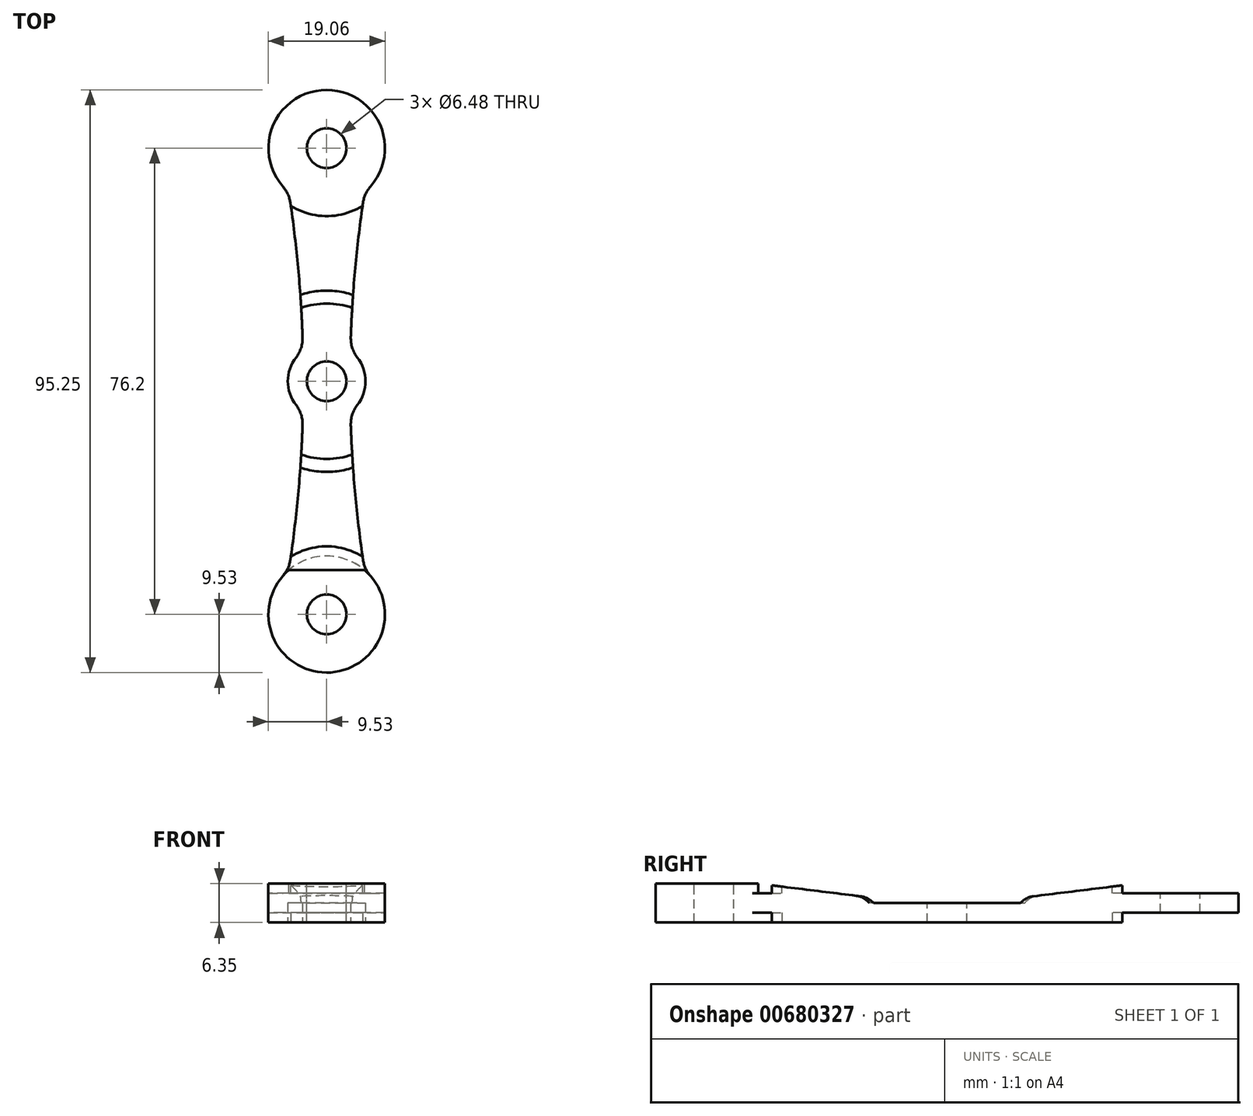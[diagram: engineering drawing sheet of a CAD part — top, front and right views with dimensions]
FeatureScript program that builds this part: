
annotation { "Feature Type Name" : "Feature", "Feature Type Description" : "" }
export const myFeature = defineFeature(function(context is Context, id is Id, definition is map)
    precondition{}
    {
        {
            var Q0;
            Q0=qCreatedBy(makeId("Top.planeOp"),FACE);
            var sketch = newSketch(context, id + "F0", { "sketchPlane" : qUnion([Q0])});
            skLineSegment(sketch, "E0.bottom", {"start": v(9.52, 47.63) * mm, "end": v(-9.53, 47.63) * mm});
            skLineSegment(sketch, "E0.top", {"start": v(9.52, -47.63) * mm, "end": v(-9.53, -47.63) * mm});
            skLineSegment(sketch, "E0.left", {"start": v(9.52, 47.63) * mm, "end": v(9.52, -47.63) * mm});
            skLineSegment(sketch, "E0.right", {"start": v(-9.52, 47.63) * mm, "end": v(-9.53, -47.63) * mm});
            skPoint(sketch, "E0.middle", {"position": v(0, 0) * mm});
            skCircle(sketch, "E1", {"center": v(0, 38.1) * mm, "radius": 9.53 * mm});
            skCircle(sketch, "E2", {"center": v(0, -38.1) * mm, "radius": 9.52 * mm});
            skCircle(sketch, "E3", {"center": v(0, 0) * mm, "radius": 6.35 * mm});
            skArc(sketch, "E4", {"start": v(-9.53, -47.62) * mm, "mid": v(-3.81, 0) * mm, "end": v(-9.53, 47.63) * mm});
            skArc(sketch, "E5", {"start": v(9.53, 47.62) * mm, "mid": v(3.81, 0) * mm, "end": v(9.53, -47.62) * mm});
            skSolve(sketch);
        }
        {
            var Q0;
            {var subQ0=sQuery(id+"F0.wireOp",EDGE,"E4");var subQ1=sQuery(id+"F0.wireOp",EDGE,"E3");var subQ2=makeQuery(id+"F0.imprint","INTERSECT",VERTEX,{"disambiguationData":[OD(0.0)],"derivedFrom":[subQ1,subQ0]});Q0=makeQuery(id+"F0.imprint","IMPRINT",FACE,{"disambiguationData":[TD([[makeQuery(id+"F0.imprint","IMPRINT",EDGE,{"disambiguationData":[TD([[subQ2,1.0]])],"derivedFrom":subQ1}),1.0]])]});}
            var Q1;
            {var subQ0=sQuery(id+"F0.wireOp",EDGE,"E5");var subQ1=sQuery(id+"F0.wireOp",EDGE,"E3");var subQ2=makeQuery(id+"F0.imprint","INTERSECT",VERTEX,{"disambiguationData":[OD(0.0)],"derivedFrom":[subQ1,subQ0]});Q1=makeQuery(id+"F0.imprint","IMPRINT",FACE,{"disambiguationData":[TD([[makeQuery(id+"F0.imprint","IMPRINT",EDGE,{"disambiguationData":[TD([[subQ2,1.0]])],"derivedFrom":subQ1}),1.0]])]});}
            var Q2;
            {var subQ0=sQuery(id+"F0.wireOp",EDGE,"E4");var subQ1=sQuery(id+"F0.wireOp",EDGE,"E3");var subQ2=makeQuery(id+"F0.imprint","INTERSECT",VERTEX,{"disambiguationData":[OD(0.0)],"derivedFrom":[subQ1,subQ0]});Q2=makeQuery(id+"F0.imprint","IMPRINT",FACE,{"disambiguationData":[TD([[makeQuery(id+"F0.imprint","IMPRINT",EDGE,{"disambiguationData":[TD([[subQ2,-1.0]])],"derivedFrom":subQ1}),1.0]])]});}
            var Q3;
            {var subQ0=sQuery(id+"F0.wireOp",EDGE,"E4");var subQ1=sQuery(id+"F0.wireOp",EDGE,"E1");var subQ2=makeQuery(id+"F0.imprint","INTERSECT",VERTEX,{"disambiguationData":[OD(1.0)],"derivedFrom":[subQ1,subQ0]});Q3=makeQuery(id+"F0.imprint","IMPRINT",FACE,{"disambiguationData":[TD([[makeQuery(id+"F0.imprint","IMPRINT",EDGE,{"disambiguationData":[TD([[subQ2,-1.0]])],"derivedFrom":subQ1}),-1.0]])]});}
            var Q4;
            {var subQ0=sQuery(id+"F0.wireOp",EDGE,"E5");var subQ1=sQuery(id+"F0.wireOp",EDGE,"E2");var subQ2=makeQuery(id+"F0.imprint","INTERSECT",VERTEX,{"disambiguationData":[OD(0.0)],"derivedFrom":[subQ1,subQ0]});Q4=makeQuery(id+"F0.imprint","IMPRINT",FACE,{"disambiguationData":[TD([[makeQuery(id+"F0.imprint","IMPRINT",EDGE,{"disambiguationData":[TD([[subQ2,-1.0]])],"derivedFrom":subQ1}),-1.0]])]});}
            var Q5;
            {var subQ0=sQuery(id+"F0.wireOp",EDGE,"E1");var subQ1=makeQuery(id+"F0.imprint","INTERSECT",VERTEX,{"derivedFrom":[sQuery(id+"F0.wireOp",EDGE,"E0.left"),subQ0]});Q5=makeQuery(id+"F0.imprint","IMPRINT",FACE,{"disambiguationData":[TD([[makeQuery(id+"F0.imprint","IMPRINT",EDGE,{"disambiguationData":[TD([[subQ1,-1.0]])],"derivedFrom":subQ0}),1.0]])]});}
            var Q6;
            {var subQ0=sQuery(id+"F0.wireOp",EDGE,"E1");var subQ1=makeQuery(id+"F0.imprint","INTERSECT",VERTEX,{"derivedFrom":[sQuery(id+"F0.wireOp",EDGE,"E0.right"),subQ0]});Q6=makeQuery(id+"F0.imprint","IMPRINT",FACE,{"disambiguationData":[TD([[makeQuery(id+"F0.imprint","IMPRINT",EDGE,{"disambiguationData":[TD([[subQ1,1.0]])],"derivedFrom":subQ0}),1.0]])]});}
            var Q7;
            {var subQ0=sQuery(id+"F0.wireOp",EDGE,"E2");var subQ1=makeQuery(id+"F0.imprint","INTERSECT",VERTEX,{"derivedFrom":[sQuery(id+"F0.wireOp",EDGE,"E0.left"),subQ0]});Q7=makeQuery(id+"F0.imprint","IMPRINT",FACE,{"disambiguationData":[TD([[makeQuery(id+"F0.imprint","IMPRINT",EDGE,{"disambiguationData":[TD([[subQ1,-1.0]])],"derivedFrom":subQ0}),1.0]])]});}
            var Q8;
            {var subQ0=sQuery(id+"F0.wireOp",EDGE,"E2");var subQ1=makeQuery(id+"F0.imprint","INTERSECT",VERTEX,{"derivedFrom":[sQuery(id+"F0.wireOp",EDGE,"E0.right"),subQ0]});Q8=makeQuery(id+"F0.imprint","IMPRINT",FACE,{"disambiguationData":[TD([[makeQuery(id+"F0.imprint","IMPRINT",EDGE,{"disambiguationData":[TD([[subQ1,1.0]])],"derivedFrom":subQ0}),1.0]])]});}
            var Q9;
            {var subQ1=sQuery(id+"F0.wireOp",EDGE,"E1");var subQ4=makeQuery(id+"F0.imprint","INTERSECT",VERTEX,{"derivedFrom":[sQuery(id+"F0.wireOp",EDGE,"E0.bottom"),subQ1]});Q9=makeQuery(id+"F0.imprint","IMPRINT",FACE,{"disambiguationData":[TD([[makeQuery(id+"F0.imprint","IMPRINT",EDGE,{"disambiguationData":[TD([[subQ4,1.0]])],"derivedFrom":subQ1}),1.0]])]});}
            var Q10;
            {var subQ1=sQuery(id+"F0.wireOp",EDGE,"E2");var subQ4=sQuery(id+"F0.wireOp",EDGE,"E5");var subQ5=makeQuery(id+"F0.imprint","INTERSECT",VERTEX,{"disambiguationData":[OD(0.0)],"derivedFrom":[subQ1,subQ4]});Q10=makeQuery(id+"F0.imprint","IMPRINT",FACE,{"disambiguationData":[TD([[makeQuery(id+"F0.imprint","IMPRINT",EDGE,{"disambiguationData":[TD([[subQ5,-1.0]])],"derivedFrom":subQ1}),1.0]])]});}
            extrude(context, id + "F1", {"entities" : qUnion([Q0, Q1, Q2, Q3, Q4, Q5, Q6, Q7, Q8, Q9, Q10]), "depth" : 6.35 * mm, "offsetDistance" : 25.4 * mm});
        }
        {
            var Q0;
            Q0=makeQuery(id+"F1.opExtrude","CAP_FACE",FACE,{"disambiguationData":[OSD([sQuery(id+"F0.wireOp",EDGE,"E1"),sQuery(id+"F0.wireOp",EDGE,"E2"),sQuery(id+"F0.wireOp",EDGE,"E3"),sQuery(id+"F0.wireOp",EDGE,"E4"),sQuery(id+"F0.wireOp",EDGE,"E5")])],"isStart":false});
            var sketch = newSketch(context, id + "F2", { "sketchPlane" : qUnion([Q0])});
            skCircle(sketch, "E6", {"center": v(0, 38.1) * mm, "radius": 3.24 * mm});
            skCircle(sketch, "E7", {"center": v(0, 0) * mm, "radius": 3.24 * mm});
            skCircle(sketch, "E8", {"center": v(0, -38.1) * mm, "radius": 3.24 * mm});
            skSolve(sketch);
        }
        {
            var Q0;
            Q0=qSketchRegion(id+"F2",true);
            extrude(context, id + "F3", {"entities" : qUnion([Q0]), "operationType" : NewBodyOperationType.REMOVE, "endBound" : BoundingType.THROUGH_ALL, "oppositeDirection" : true, "depth" : 25.4 * mm, "offsetDistance" : 25.4 * mm});
        }
        {
            var Q0;
            Q0=qCreatedBy(makeId("Right.planeOp"),FACE);
            var sketch = newSketch(context, id + "F4", { "sketchPlane" : qUnion([Q0])});
            skPoint(sketch, "E9.0", {"position": v(-30.86, 6.35) * mm});
            skPoint(sketch, "E10.0", {"position": v(30.86, 6.35) * mm});
            skLineSegment(sketch, "E11", {"start": v(-30.86, 6.35) * mm, "end": v(30.86, 6.35) * mm});
            skPoint(sketch, "E12.0", {"position": v(-5.03, 3.18) * mm});
            skPoint(sketch, "E13.0", {"position": v(5.03, 3.18) * mm});
            skLineSegment(sketch, "E14", {"start": v(-30.86, 6.35) * mm, "end": v(-5.03, 3.18) * mm});
            skLineSegment(sketch, "E15", {"start": v(5.03, 3.18) * mm, "end": v(30.86, 6.35) * mm});
            skLineSegment(sketch, "E16", {"start": v(-5.03, 3.18) * mm, "end": v(5.03, 3.18) * mm});
            skSolve(sketch);
        }
        {
            var Q0;
            Q0=qSketchRegion(id+"F4",true);
            extrude(context, id + "F5", {"entities" : qUnion([Q0]), "operationType" : NewBodyOperationType.REMOVE, "oppositeDirection" : true, "depth" : 25.4 * mm, "offsetDistance" : 25.4 * mm, "hasSecondDirection" : true, "secondDirectionOppositeDirection" : false, "secondDirectionDepth" : 25.4 * mm});
        }
        {
            var Q0;
            Q0=makeQuery(id+"F5.boolean.opBoolean","COPY",EDGE,{"derivedFrom":makeQuery(id+"F5.opExtrude","SWEPT_EDGE",EDGE,{"disambiguationData":[OSD([sQuery(id+"F4.wireOp",EDGE,"E11"),sQuery(id+"F4.wireOp",EDGE,"E14")])]})});
            var Q1;
            Q1=makeQuery(id+"F5.boolean.opBoolean","COPY",EDGE,{"derivedFrom":makeQuery(id+"F5.opExtrude","SWEPT_EDGE",EDGE,{"disambiguationData":[OSD([sQuery(id+"F4.wireOp",EDGE,"E11"),sQuery(id+"F4.wireOp",EDGE,"E15")])]})});
            var Q2;
            Q2=makeQuery(id+"F5.boolean.opBoolean","COPY",EDGE,{"derivedFrom":makeQuery(id+"F5.opExtrude","SWEPT_EDGE",EDGE,{"disambiguationData":[OSD([sQuery(id+"F4.wireOp",EDGE,"E14"),sQuery(id+"F4.wireOp",EDGE,"E16")])]})});
            var Q3;
            Q3=makeQuery(id+"F5.boolean.opBoolean","COPY",EDGE,{"derivedFrom":makeQuery(id+"F5.opExtrude","SWEPT_EDGE",EDGE,{"disambiguationData":[OSD([sQuery(id+"F4.wireOp",EDGE,"E15"),sQuery(id+"F4.wireOp",EDGE,"E16")])]})});
            var Q4;
            {var subQ0=sQuery(id+"F0.wireOp",EDGE,"E5");var subQ1=sQuery(id+"F0.wireOp",EDGE,"E3");Q4=makeQuery(id+"F1.opExtrude","SWEPT_EDGE",EDGE,{"disambiguationData":[OSD([subQ1,subQ0]),TDD([makeQuery(id+"F0.imprint","INTERSECT",VERTEX,{"disambiguationData":[OD(0.0)],"derivedFrom":[subQ1,subQ0]})])]});}
            var Q5;
            {var subQ0=sQuery(id+"F0.wireOp",EDGE,"E5");var subQ1=sQuery(id+"F0.wireOp",EDGE,"E3");Q5=makeQuery(id+"F1.opExtrude","SWEPT_EDGE",EDGE,{"disambiguationData":[OSD([subQ1,subQ0]),TDD([makeQuery(id+"F0.imprint","INTERSECT",VERTEX,{"disambiguationData":[OD(1.0)],"derivedFrom":[subQ1,subQ0]})])]});}
            var Q6;
            {var subQ0=sQuery(id+"F0.wireOp",EDGE,"E4");var subQ1=sQuery(id+"F0.wireOp",EDGE,"E3");Q6=makeQuery(id+"F1.opExtrude","SWEPT_EDGE",EDGE,{"disambiguationData":[OSD([subQ1,subQ0]),TDD([makeQuery(id+"F0.imprint","INTERSECT",VERTEX,{"disambiguationData":[OD(1.0)],"derivedFrom":[subQ1,subQ0]})])]});}
            var Q7;
            {var subQ0=sQuery(id+"F0.wireOp",EDGE,"E4");var subQ1=sQuery(id+"F0.wireOp",EDGE,"E3");Q7=makeQuery(id+"F1.opExtrude","SWEPT_EDGE",EDGE,{"disambiguationData":[OSD([subQ1,subQ0]),TDD([makeQuery(id+"F0.imprint","INTERSECT",VERTEX,{"disambiguationData":[OD(0.0)],"derivedFrom":[subQ1,subQ0]})])]});}
            var Q8;
            Q8=makeQuery(id+"F1.opExtrude","SWEPT_EDGE",EDGE,{"disambiguationData":[OSD([sQuery(id+"F0.wireOp",EDGE,"E2"),sQuery(id+"F0.wireOp",EDGE,"E4")])]});
            var Q9;
            Q9=makeQuery(id+"F1.opExtrude","SWEPT_EDGE",EDGE,{"disambiguationData":[OSD([sQuery(id+"F0.wireOp",EDGE,"E1"),sQuery(id+"F0.wireOp",EDGE,"E4")])]});
            var Q10;
            Q10=makeQuery(id+"F1.opExtrude","SWEPT_EDGE",EDGE,{"disambiguationData":[OSD([sQuery(id+"F0.wireOp",EDGE,"E1"),sQuery(id+"F0.wireOp",EDGE,"E5")])]});
            var Q11;
            Q11=makeQuery(id+"F1.opExtrude","SWEPT_EDGE",EDGE,{"disambiguationData":[OSD([sQuery(id+"F0.wireOp",EDGE,"E2"),sQuery(id+"F0.wireOp",EDGE,"E5")])]});
            fillet(context, id + "F6", {"entities" : qUnion([Q0, Q1, Q2, Q3, Q4, Q5, Q6, Q7, Q8, Q9, Q10, Q11]), "radius" : 5.08 * mm, "tangentPropagation" : true, "allowEdgeOverflow" : false});
        }
        {
            var Q0;
            {var subQ0=sQuery(id+"F0.wireOp",EDGE,"E5");var subQ1=sQuery(id+"F0.wireOp",EDGE,"E2");var subQ2=sQuery(id+"F0.wireOp",EDGE,"E3");var subQ3=sQuery(id+"F0.wireOp",EDGE,"E4");Q0=makeQuery(id+"F5.boolean.opBoolean","SPLIT",FACE,{"disambiguationData":[TD([makeQuery(id+"F1.opExtrude","SWEPT_FACE",FACE,{"disambiguationData":[OSD([subQ1])]})])],"derivedFrom":makeQuery(id+"F1.opExtrude","CAP_FACE",FACE,{"disambiguationData":[OSD([sQuery(id+"F0.wireOp",EDGE,"E1"),subQ1,subQ2,subQ3,subQ0])],"isStart":false})});}
            var sketch = newSketch(context, id + "F7", { "sketchPlane" : qUnion([Q0])});
            skCircle(sketch, "E17", {"center": v(0, -38.1) * mm, "radius": 9.52 * mm});
            skArc(sketch, "E18.0", {"start": v(7.15, 31.8) * mm, "mid": v(0, 47.63) * mm, "end": v(-7.15, 31.8) * mm});
            skCircle(sketch, "E19", {"center": v(0, 38.1) * mm, "radius": 9.53 * mm});
            skCircle(sketch, "E20", {"center": v(0, -38.1) * mm, "radius": 11.11 * mm});
            skCircle(sketch, "E21", {"center": v(0, 38.1) * mm, "radius": 11.11 * mm});
            skSolve(sketch);
        }
        {
            var Q0;
            Q0 = qSketchRegion(id + "F7", true);
            var Q1;
            {var subQ0=sQuery(id+"F2.wireOp",EDGE,"E8");Q1=makeQuery(id+"F7.imprint","IMPRINT",FACE,{"disambiguationData":[TD([[makeQuery(id+"F7.imprint","IMPRINT",EDGE,{"derivedFrom":makeQuery(id+"F3.boolean.opBoolean","COPY",EDGE,{"derivedFrom":makeQuery(id+"F3.opExtrude","CAP_EDGE",EDGE,{"disambiguationData":[OSD([subQ0])],"isStart":true})})}),-1.0]])]});}
            var Q2;
            {var subQ0=sQuery(id+"F7.wireOp",EDGE,"E17");var subQ1=sQuery(id+"F0.wireOp",EDGE,"E5");var subQ2=sQuery(id+"F0.wireOp",EDGE,"E2");var subQ3=sQuery(id+"F0.wireOp",EDGE,"E3");var subQ4=sQuery(id+"F0.wireOp",EDGE,"E4");var subQ5=sQuery(id+"F4.wireOp",EDGE,"E14");var subQ6=makeQuery(id+"F6.opFillet","BLEND_EDGE",EDGE,{"blendedFrom":[makeQuery(id+"F5.boolean.opBoolean","COPY",EDGE,{"derivedFrom":makeQuery(id+"F5.opExtrude","SWEPT_EDGE",EDGE,{"disambiguationData":[OSD([sQuery(id+"F4.wireOp",EDGE,"E11"),subQ5])]})}),makeQuery(id+"F5.boolean.opBoolean","SPLIT",FACE,{"disambiguationData":[TD([makeQuery(id+"F1.opExtrude","SWEPT_FACE",FACE,{"disambiguationData":[OSD([subQ2])]})])],"derivedFrom":makeQuery(id+"F1.opExtrude","CAP_FACE",FACE,{"disambiguationData":[OSD([sQuery(id+"F0.wireOp",EDGE,"E1"),subQ2,subQ3,subQ4,subQ1])],"isStart":false})})],"blendedInto":[makeQuery(id+"F5.boolean.opBoolean","SPLIT",FACE,{"disambiguationData":[TD([makeQuery(id+"F1.opExtrude","SWEPT_FACE",FACE,{"disambiguationData":[OSD([subQ2])]})])],"derivedFrom":makeQuery(id+"F1.opExtrude","CAP_FACE",FACE,{"disambiguationData":[OSD([sQuery(id+"F0.wireOp",EDGE,"E1"),subQ2,subQ3,subQ4,subQ1])],"isStart":false})})]});var subQ7=makeQuery(id+"F7.imprint","INTERSECT",VERTEX,{"disambiguationData":[OD(0.0)],"derivedFrom":[subQ6,subQ0]});Q2=makeQuery(id+"F7.imprint","IMPRINT",FACE,{"disambiguationData":[TD([[makeQuery(id+"F7.imprint","IMPRINT",EDGE,{"disambiguationData":[TD([[subQ7,-1.0]])],"derivedFrom":subQ0}),1.0]])]});}
            var Q3;
            {var subQ0=sQuery(id+"F7.wireOp",EDGE,"E19");var subQ1=makeQuery(id+"F7.imprint","IMPRINT",VERTEX,{"disambiguationData":[OD(0.0)],"derivedFrom":subQ0});Q3=makeQuery(id+"F7.imprint","IMPRINT",FACE,{"disambiguationData":[TD([[makeQuery(id+"F7.imprint","IMPRINT",EDGE,{"disambiguationData":[TD([[subQ1,-1.0]])],"derivedFrom":subQ0}),1.0]])]});}
            extrude(context, id + "F8", {"entities" : qUnion([Q0, Q1, Q2, Q3]), "operationType" : NewBodyOperationType.REMOVE, "oppositeDirection" : true, "depth" : 1.59 * mm, "offsetDistance" : 25.4 * mm});
        }
        {
            var Q0;
            Q0=makeQuery(id+"F1.opExtrude","CAP_FACE",FACE,{"disambiguationData":[OSD([sQuery(id+"F0.wireOp",EDGE,"E1"),sQuery(id+"F0.wireOp",EDGE,"E2"),sQuery(id+"F0.wireOp",EDGE,"E3"),sQuery(id+"F0.wireOp",EDGE,"E4"),sQuery(id+"F0.wireOp",EDGE,"E5")])],"isStart":true});
            var sketch = newSketch(context, id + "F9", { "sketchPlane" : qUnion([Q0])});
            skArc(sketch, "E22.0", {"start": v(-7.15, 31.8) * mm, "mid": v(0, 47.63) * mm, "end": v(7.15, 31.8) * mm});
            skArc(sketch, "E23.0", {"start": v(7.15, -31.8) * mm, "mid": v(0, -47.63) * mm, "end": v(-7.15, -31.8) * mm});
            skCircle(sketch, "E24", {"center": v(0, 38.1) * mm, "radius": 9.52 * mm});
            skCircle(sketch, "E25", {"center": v(0, -38.1) * mm, "radius": 9.53 * mm});
            skCircle(sketch, "E26", {"center": v(0, 38.1) * mm, "radius": 11.11 * mm});
            skCircle(sketch, "E27", {"center": v(0, -38.1) * mm, "radius": 11.11 * mm});
            skSolve(sketch);
        }
        {
            var Q0;
            Q0 = qSketchRegion(id + "F9", true);
            var Q1;
            {var subQ0=sQuery(id+"F9.wireOp",EDGE,"E24");Q1=makeQuery(id+"F9.imprint","IMPRINT",FACE,{"disambiguationData":[TD([[makeQuery(id+"F9.imprint","IMPRINT",EDGE,{"disambiguationData":[OD(0.0)],"derivedFrom":subQ0}),-1.0]])]});}
            var Q2;
            Q2=makeQuery(id+"F9.imprint","IMPRINT",FACE,{"disambiguationData":[TD([[makeQuery(id+"F9.imprint","IMPRINT",EDGE,{"derivedFrom":makeQuery(id+"F3.boolean.opBoolean","INTERSECT",EDGE,{"derivedFrom":[makeQuery(id+"F1.opExtrude","CAP_FACE",FACE,{"disambiguationData":[OSD([sQuery(id+"F0.wireOp",EDGE,"E1"),sQuery(id+"F0.wireOp",EDGE,"E2"),sQuery(id+"F0.wireOp",EDGE,"E3"),sQuery(id+"F0.wireOp",EDGE,"E4"),sQuery(id+"F0.wireOp",EDGE,"E5")])],"isStart":true}),makeQuery(id+"F3.opExtrude","SWEPT_FACE",FACE,{"disambiguationData":[OSD([sQuery(id+"F2.wireOp",EDGE,"E8")])]})]})}),-1.0]])]});
            var Q3;
            Q3=makeQuery(id+"F9.imprint","IMPRINT",FACE,{"disambiguationData":[TD([[makeQuery(id+"F9.imprint","IMPRINT",EDGE,{"derivedFrom":makeQuery(id+"F3.boolean.opBoolean","INTERSECT",EDGE,{"derivedFrom":[makeQuery(id+"F1.opExtrude","CAP_FACE",FACE,{"disambiguationData":[OSD([sQuery(id+"F0.wireOp",EDGE,"E1"),sQuery(id+"F0.wireOp",EDGE,"E2"),sQuery(id+"F0.wireOp",EDGE,"E3"),sQuery(id+"F0.wireOp",EDGE,"E4"),sQuery(id+"F0.wireOp",EDGE,"E5")])],"isStart":true}),makeQuery(id+"F3.opExtrude","SWEPT_FACE",FACE,{"disambiguationData":[OSD([sQuery(id+"F2.wireOp",EDGE,"E6")])]})]})}),-1.0]])]});
            var Q4;
            {var subQ0=sQuery(id+"F9.wireOp",EDGE,"E25");Q4=makeQuery(id+"F9.imprint","IMPRINT",FACE,{"disambiguationData":[TD([[makeQuery(id+"F9.imprint","IMPRINT",EDGE,{"disambiguationData":[OD(0.0)],"derivedFrom":subQ0}),1.0]])]});}
            extrude(context, id + "F10", {"entities" : qUnion([Q0, Q1, Q2, Q3, Q4]), "operationType" : NewBodyOperationType.REMOVE, "oppositeDirection" : true, "depth" : 1.59 * mm, "offsetDistance" : 25.4 * mm});
        }
        {
            var Q0;
            Q0=makeQuery(id+"F5.boolean.opBoolean","COPY",FACE,{"derivedFrom":makeQuery(id+"F5.opExtrude","SWEPT_FACE",FACE,{"disambiguationData":[OSD([sQuery(id+"F4.wireOp",EDGE,"E16")])]})});
            var sketch = newSketch(context, id + "F11", { "sketchPlane" : qUnion([Q0])});
            skCircle(sketch, "E28.0", {"center": v(0, 0) * mm, "radius": 3.24 * mm});
            skCircle(sketch, "E29", {"center": v(0, 0) * mm, "radius": 12.7 * mm});
            skSolve(sketch);
        }
        {
            var Q0;
            Q0 = qSketchRegion(id + "F11", true);
            extrude(context, id + "F12", {"entities" : qUnion([Q0]), "operationType" : NewBodyOperationType.REMOVE, "depth" : 25.4 * mm, "offsetDistance" : 25.4 * mm});
        }
        {
            var Q0;
            Q0=makeQuery(id+"F12.boolean.opBoolean","INTERSECT",EDGE,{"derivedFrom":[makeQuery(id+"F5.boolean.opBoolean","COPY",FACE,{"derivedFrom":makeQuery(id+"F5.opExtrude","SWEPT_FACE",FACE,{"disambiguationData":[OSD([sQuery(id+"F4.wireOp",EDGE,"E15")])]})}),makeQuery(id+"F12.opExtrude","SWEPT_FACE",FACE,{"disambiguationData":[OSD([sQuery(id+"F11.wireOp",EDGE,"E29")])]})]});
            var Q1;
            Q1=makeQuery(id+"F12.boolean.opBoolean","INTERSECT",EDGE,{"derivedFrom":[makeQuery(id+"F5.boolean.opBoolean","COPY",FACE,{"derivedFrom":makeQuery(id+"F5.opExtrude","SWEPT_FACE",FACE,{"disambiguationData":[OSD([sQuery(id+"F4.wireOp",EDGE,"E14")])]})}),makeQuery(id+"F12.opExtrude","SWEPT_FACE",FACE,{"disambiguationData":[OSD([sQuery(id+"F11.wireOp",EDGE,"E29")])]})]});
            fillet(context, id + "F13", {"entities" : qUnion([Q0, Q1]), "radius" : 3.17 * mm, "tangentPropagation" : true, "allowEdgeOverflow" : false});
        }
    });
